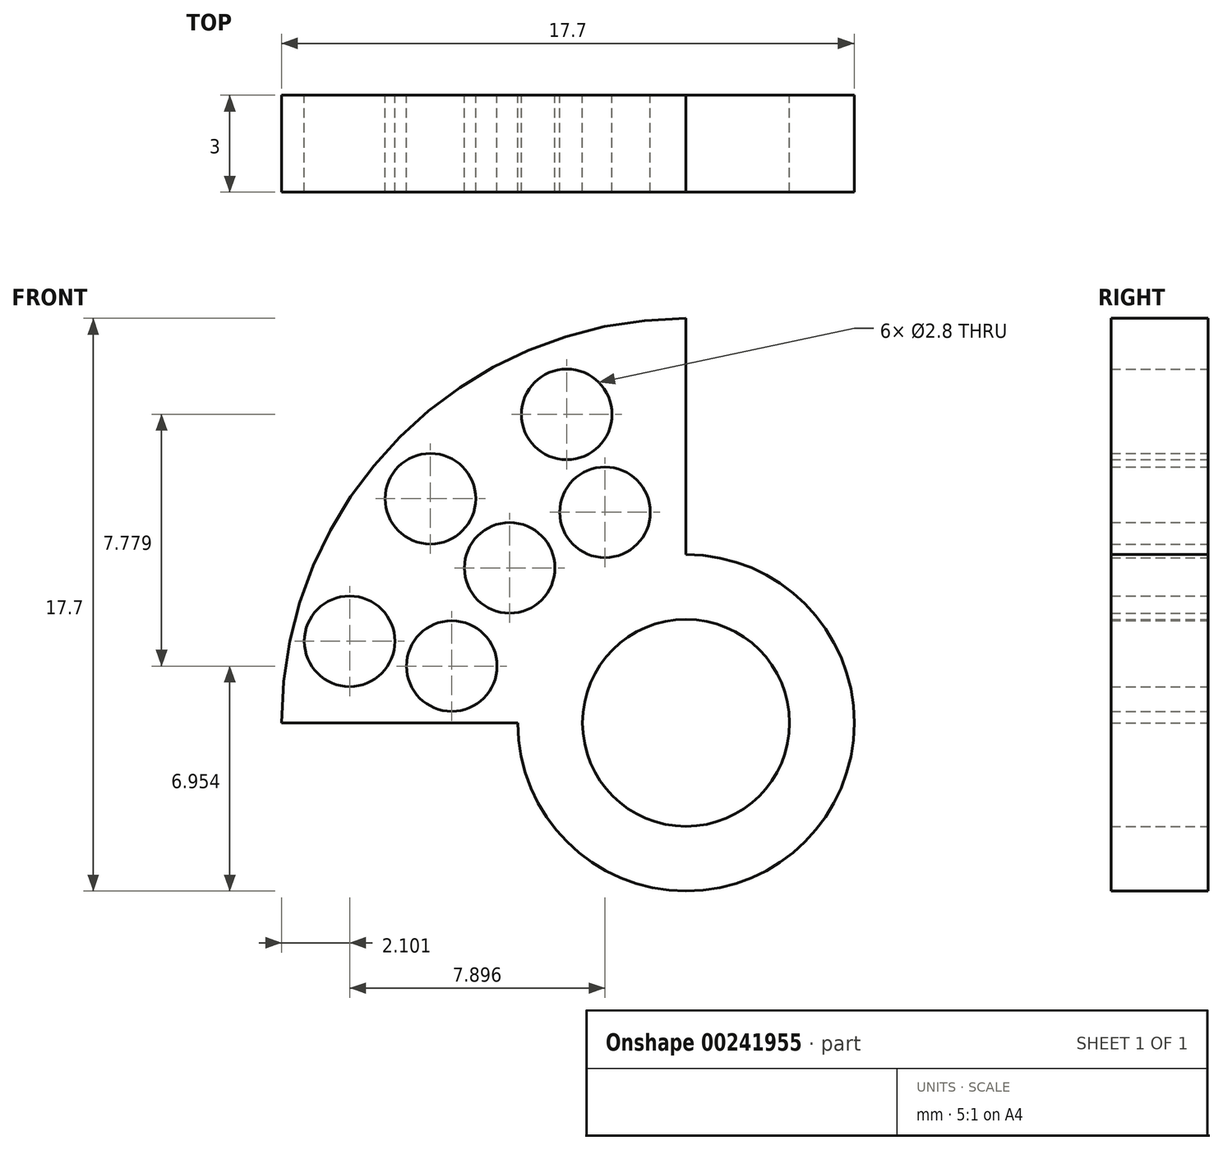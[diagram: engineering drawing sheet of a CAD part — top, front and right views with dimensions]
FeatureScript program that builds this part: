
annotation { "Feature Type Name" : "Feature", "Feature Type Description" : "" }
export const myFeature = defineFeature(function(context is Context, id is Id, definition is map)
    precondition{}
    {
        {
            var Q0;
            Q0=qCreatedBy(makeId("Front.planeOp"),FACE);
            var sketch = newSketch(context, id + "F0", { "sketchPlane" : qUnion([Q0])});
            skCircle(sketch, "E0", {"center": v(0, 0) * mm, "radius": 3.2 * mm});
            skCircle(sketch, "E1", {"center": v(0, 0) * mm, "radius": 12.5 * mm});
            skLineSegment(sketch, "E2", {"start": v(-3.2, 0) * mm, "end": v(-12.5, 0) * mm});
            skLineSegment(sketch, "E3", {"start": v(0, 0) * mm, "end": v(0, 12.5) * mm});
            skLineSegment(sketch, "E4", {"start": v(0, 0) * mm, "end": v(-12.15, 2.94) * mm, "construction": true});
            skLineSegment(sketch, "E5.1.0", {"start": v(0, 0) * mm, "end": v(-9.42, 8.22) * mm, "construction": true});
            skLineSegment(sketch, "E5.2.0", {"start": v(0, 0) * mm, "end": v(-4.56, 11.64) * mm, "construction": true});
            skLineSegment(sketch, "E5.anchor2", {"start": v(0, 0) * mm, "end": v(-4.56, 11.64) * mm, "construction": true});
            skCircle(sketch, "E6", {"center": v(-7.24, 1.75) * mm, "radius": 1.4 * mm});
            skCircle(sketch, "E7", {"center": v(-10.4, 2.52) * mm, "radius": 1.4 * mm});
            skCircle(sketch, "E8.1.0", {"center": v(-7.9, 6.93) * mm, "radius": 1.4 * mm});
            skCircle(sketch, "E8.1.1", {"center": v(-5.45, 4.79) * mm, "radius": 1.4 * mm});
            skCircle(sketch, "E8.2.0", {"center": v(-3.69, 9.53) * mm, "radius": 1.4 * mm});
            skCircle(sketch, "E8.2.1", {"center": v(-2.5, 6.5) * mm, "radius": 1.4 * mm});
            skPoint(sketch, "E8.center", {"position": v(0.05, -0.01) * mm});
            skLineSegment(sketch, "E8.anchor1", {"start": v(0.05, -0.01) * mm, "end": v(-10.4, 2.52) * mm, "construction": true});
            skLineSegment(sketch, "E8.anchor2", {"start": v(0.05, -0.01) * mm, "end": v(-3.69, 9.53) * mm, "construction": true});
            skCircle(sketch, "E9.0", {"center": v(0, 0) * mm, "radius": 5.2 * mm});
            skSolve(sketch);
        }
        {
            var Q0;
            {var subQ0=sQuery(id+"F0.wireOp",EDGE,"E2");Q0=makeQuery(id+"F0.imprint","IMPRINT",FACE,{"disambiguationData":[TD([[makeQuery(id+"F0.imprint","IMPRINT",EDGE,{"derivedFrom":subQ0}),-1.0]])]});}
            var Q1;
            Q1=makeQuery(id+"F0.imprint","IMPRINT",FACE,{"disambiguationData":[TD([[makeQuery(id+"F0.imprint","IMPRINT",EDGE,{"derivedFrom":sQuery(id+"F0.wireOp",EDGE,"E6")}),-1.0]])]});
            var Q2;
            {var subQ0=sQuery(id+"F0.wireOp",EDGE,"E2");var subQ1=sQuery(id+"F0.wireOp",EDGE,"E0");var subQ2=makeQuery(id+"F0.imprint","INTERSECT",VERTEX,{"derivedFrom":[subQ1,subQ0]});Q2=makeQuery(id+"F0.imprint","IMPRINT",FACE,{"disambiguationData":[TD([[makeQuery(id+"F0.imprint","IMPRINT",EDGE,{"disambiguationData":[TD([[subQ2,-1.0]])],"derivedFrom":subQ1}),-1.0]])]});}
            extrude(context, id + "F1", {"entities" : qUnion([Q0, Q1, Q2]), "depth" : 3 * mm});
        }
    });
